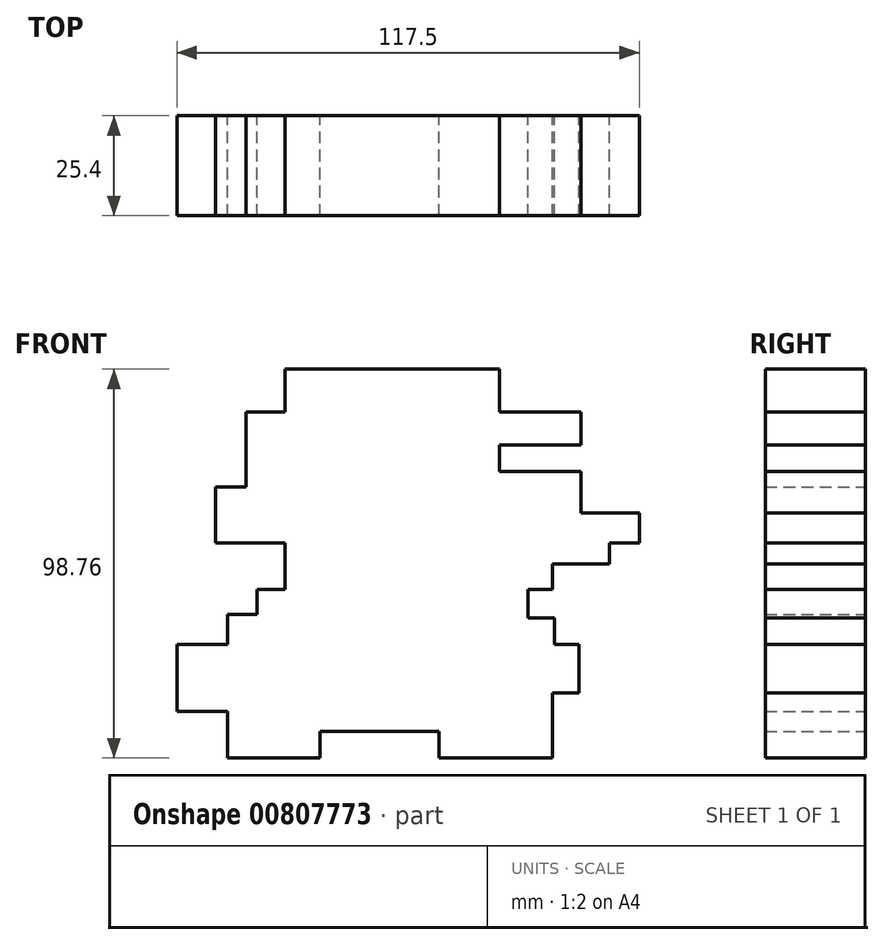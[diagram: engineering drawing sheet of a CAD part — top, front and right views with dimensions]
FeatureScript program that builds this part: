
annotation { "Feature Type Name" : "Feature", "Feature Type Description" : "" }
export const myFeature = defineFeature(function(context is Context, id is Id, definition is map)
    precondition{}
    {
        {
            var Q0;
            Q0=qCreatedBy(makeId("Front.planeOp"),FACE);
            var sketch = newSketch(context, id + "F0", { "sketchPlane" : qUnion([Q0])});
            skLineSegment(sketch, "E0", {"start": v(-38.47, 25.6) * mm, "end": v(-38.47, 17.2) * mm});
            skLineSegment(sketch, "E1", {"start": v(-38.47, 25.6) * mm, "end": v(-28.67, 25.6) * mm});
            skLineSegment(sketch, "E2", {"start": v(-28.67, 25.6) * mm, "end": v(-28.67, 36.5) * mm});
            skLineSegment(sketch, "E3", {"start": v(-28.67, 36.5) * mm, "end": v(25.88, 36.5) * mm});
            skLineSegment(sketch, "E4", {"start": v(25.88, 36.5) * mm, "end": v(25.88, 25.6) * mm});
            skLineSegment(sketch, "E5", {"start": v(25.88, 25.6) * mm, "end": v(46.58, 25.6) * mm});
            skLineSegment(sketch, "E6", {"start": v(46.58, 25.6) * mm, "end": v(46.58, 17.2) * mm});
            skLineSegment(sketch, "E7", {"start": v(46.58, 17.2) * mm, "end": v(25.88, 17.2) * mm});
            skLineSegment(sketch, "E8", {"start": v(-38.47, 17.2) * mm, "end": v(-38.47, 6.57) * mm});
            skLineSegment(sketch, "E9", {"start": v(-38.47, 6.57) * mm, "end": v(-46.3, 6.57) * mm});
            skLineSegment(sketch, "E10", {"start": v(-46.3, 6.57) * mm, "end": v(-46.3, -7.7) * mm});
            skLineSegment(sketch, "E11", {"start": v(-46.3, -7.7) * mm, "end": v(-28.67, -7.7) * mm});
            skLineSegment(sketch, "E12", {"start": v(-28.67, -7.7) * mm, "end": v(-28.67, -19.44) * mm});
            skLineSegment(sketch, "E13", {"start": v(-28.67, -19.44) * mm, "end": v(-35.67, -19.44) * mm});
            skLineSegment(sketch, "E14", {"start": v(-35.67, -19.44) * mm, "end": v(-35.67, -25.88) * mm});
            skLineSegment(sketch, "E15", {"start": v(-35.67, -25.88) * mm, "end": v(-43.22, -25.88) * mm});
            skLineSegment(sketch, "E16", {"start": v(-43.22, -25.88) * mm, "end": v(-43.22, -33.43) * mm});
            skLineSegment(sketch, "E17", {"start": v(-43.22, -33.43) * mm, "end": v(-56.1, -33.43) * mm});
            skLineSegment(sketch, "E18", {"start": v(-56.1, -33.43) * mm, "end": v(-56.1, -50.5) * mm});
            skLineSegment(sketch, "E19", {"start": v(-56.1, -50.5) * mm, "end": v(-43.22, -50.5) * mm});
            skLineSegment(sketch, "E20", {"start": v(39.3, -19.44) * mm, "end": v(39.3, -13) * mm});
            skLineSegment(sketch, "E21", {"start": v(39.3, -13) * mm, "end": v(53.85, -13) * mm});
            skLineSegment(sketch, "E22", {"start": v(53.85, -13) * mm, "end": v(53.85, -7.7) * mm});
            skLineSegment(sketch, "E23", {"start": v(25.88, 17.2) * mm, "end": v(25.88, 10.5) * mm});
            skLineSegment(sketch, "E24", {"start": v(25.88, 10.5) * mm, "end": v(46.58, 10.5) * mm});
            skPoint(sketch, "E24.endSnap0", {"position": v(46.58, -13) * mm});
            skLineSegment(sketch, "E25", {"start": v(46.58, 10.5) * mm, "end": v(46.58, 0) * mm});
            skLineSegment(sketch, "E26", {"start": v(46.58, 0) * mm, "end": v(61.4, 0) * mm});
            skLineSegment(sketch, "E27", {"start": v(61.4, 0) * mm, "end": v(61.4, -7.7) * mm});
            skLineSegment(sketch, "E28", {"start": v(61.4, -7.7) * mm, "end": v(53.85, -7.7) * mm});
            skLineSegment(sketch, "E29", {"start": v(-43.22, -50.5) * mm, "end": v(-43.22, -62.25) * mm});
            skLineSegment(sketch, "E30", {"start": v(-43.22, -62.25) * mm, "end": v(-19.72, -62.25) * mm});
            skLineSegment(sketch, "E31", {"start": v(-19.72, -62.25) * mm, "end": v(-19.72, -55.53) * mm});
            skLineSegment(sketch, "E32", {"start": v(-19.72, -55.53) * mm, "end": v(10.5, -55.53) * mm});
            skLineSegment(sketch, "E33", {"start": v(10.5, -55.53) * mm, "end": v(10.5, -62.25) * mm});
            skLineSegment(sketch, "E34", {"start": v(10.5, -62.25) * mm, "end": v(39.3, -62.25) * mm});
            skLineSegment(sketch, "E35", {"start": v(39.3, -62.25) * mm, "end": v(39.3, -45.74) * mm});
            skLineSegment(sketch, "E36", {"start": v(33.15, -19.44) * mm, "end": v(33.15, -26.72) * mm});
            skLineSegment(sketch, "E37", {"start": v(33.15, -26.72) * mm, "end": v(39.87, -26.72) * mm});
            skLineSegment(sketch, "E38", {"start": v(39.87, -26.72) * mm, "end": v(39.87, -33.43) * mm});
            skLineSegment(sketch, "E39", {"start": v(39.87, -33.43) * mm, "end": v(46.02, -33.43) * mm});
            skLineSegment(sketch, "E40", {"start": v(46.02, -33.43) * mm, "end": v(46.02, -45.74) * mm});
            skLineSegment(sketch, "E41", {"start": v(46.02, -45.74) * mm, "end": v(39.3, -45.74) * mm});
            skPoint(sketch, "E42.end.orphan", {"position": v(-19.72, 6.57) * mm});
            skPoint(sketch, "E43.end.orphan", {"position": v(-19.72, 3.22) * mm});
            skPoint(sketch, "E44.end.orphan", {"position": v(-19.72, -2.38) * mm});
            skPoint(sketch, "E45.end.orphan", {"position": v(-25.88, 6.57) * mm});
            skPoint(sketch, "E46.start.orphan", {"position": v(-31.75, 6.57) * mm});
            skPoint(sketch, "E47.end.orphan", {"position": v(-31.75, -7.7) * mm});
            skLineSegment(sketch, "E48.trimOffspring", {"start": v(33.15, -19.44) * mm, "end": v(39.3, -19.44) * mm});
            skPoint(sketch, "E49.end.orphan", {"position": v(-13, -19.44) * mm});
            skPoint(sketch, "E50.end.orphan", {"position": v(-21.68, -33.43) * mm});
            skPoint(sketch, "E51.end.orphan", {"position": v(-35.67, -33.43) * mm});
            skPoint(sketch, "E52.start.orphan", {"position": v(-43.22, -40.7) * mm});
            skPoint(sketch, "E53.start.orphan", {"position": v(-35.67, -45.74) * mm});
            skPoint(sketch, "E54.end.orphan", {"position": v(-21.68, -37.9) * mm});
            skPoint(sketch, "E54.start.orphan", {"position": v(-21.68, -43.22) * mm});
            skPoint(sketch, "E55.end.orphan", {"position": v(16.65, -37.9) * mm});
            skPoint(sketch, "E56.end.orphan", {"position": v(16.65, -33.43) * mm});
            skPoint(sketch, "E57.end.orphan", {"position": v(32.6, -33.43) * mm});
            skPoint(sketch, "E58.start.orphan", {"position": v(24.48, -26.72) * mm});
            skPoint(sketch, "E59.end.orphan", {"position": v(10.5, -13) * mm});
            skPoint(sketch, "E60.end.orphan", {"position": v(18.32, -7.7) * mm});
            skPoint(sketch, "E61.end.orphan", {"position": v(11.89, 0) * mm});
            skPoint(sketch, "E62.end.orphan", {"position": v(18.32, 11.33) * mm});
            skPoint(sketch, "E63.end.orphan", {"position": v(18.32, 0) * mm});
            skPoint(sketch, "E64.end.orphan", {"position": v(25.88, 0) * mm});
            skPoint(sketch, "E65.end.orphan", {"position": v(25.88, -7.7) * mm});
            skSolve(sketch);
        }
        {
            var Q0;
            Q0=makeQuery(id+"F0.imprint","IMPRINT",FACE,{"disambiguationData":[TD([[makeQuery(id+"F0.imprint","IMPRINT",EDGE,{"derivedFrom":sQuery(id+"F0.wireOp",EDGE,"E0")}),1.0]])]});
            extrude(context, id + "F1", {"entities" : qUnion([Q0]), "depth" : 25.4 * mm, "offsetDistance" : 25.4 * mm});
        }
    });
